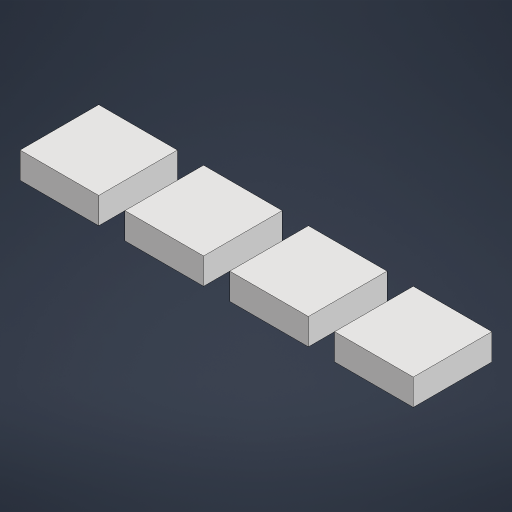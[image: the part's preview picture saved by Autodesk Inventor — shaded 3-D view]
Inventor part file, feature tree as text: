
AUTODESK INVENTOR PART (.ipt)
format: ipt  version: 2023.1 (Build 271208000, 208)  size: 185,856 bytes
history: native  units: in
note: dims shown in document units (in); Inventor stores cm internally (conversion verified against a paired STEP export)
features: move_body x4, imported_body x4, other x3, extrude x1, sketch x1
ambient origin geometry x8: Origin, YZ Plane, XZ Plane, XY Plane, X Axis, Y Axis, Z Axis, Center Point
bodies: Solid1 (feature_tree), Solid2 (feature_tree), Solid3 (feature_tree), Solid4 (feature_tree), Solid5 (feature_tree)
feature tree (13):
  other  "Repaired Geometry1"
  other  "Repaired Geometry2"
  other  "Repaired Geometry3"
  extrude  "Extrusion1"  Depth=9.0in
  move_body  "Move Body1"
  move_body  "Move Body2"
  move_body  "Move Body3"
  move_body  "Move Body4"
  sketch  "Sketch2"  dims[d3=9.0in d4=9.0in d5=3.0in d6=0.0in d7=12.0in d8=0.0in d9=0.0in d10=12.0in d11=0.0in d12=0.0in d13=-12.0in d14=0.0in d15=0.0in d16=12.0in d17=0.0in d18=0.0in]
  imported_body  "Base1"
  imported_body  "Base2"
  imported_body  "Base3"
  imported_body  "Base4"
